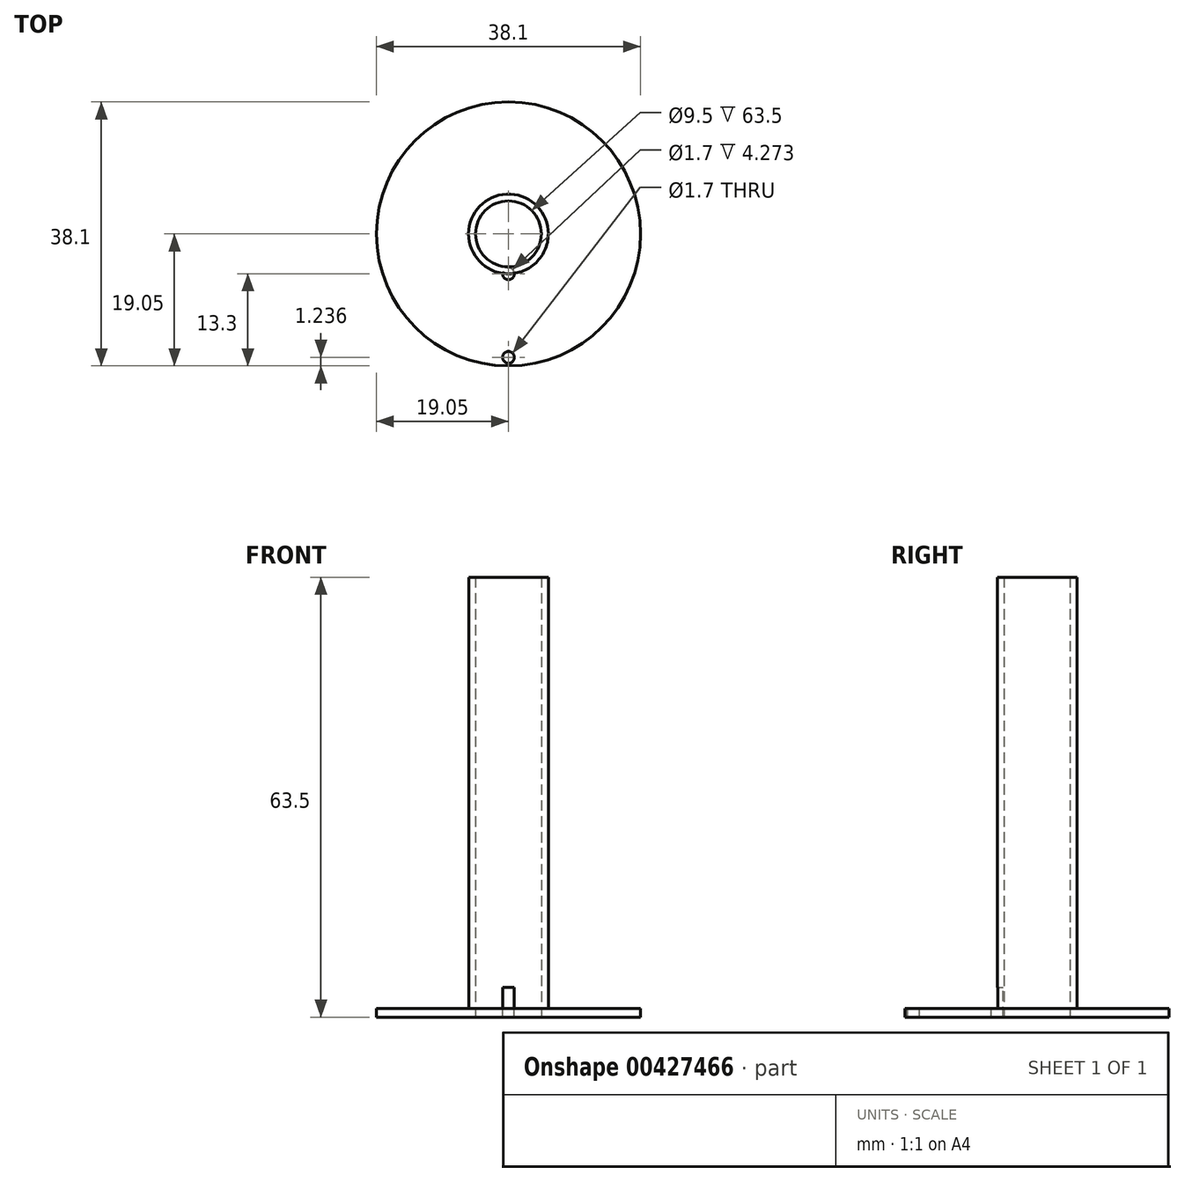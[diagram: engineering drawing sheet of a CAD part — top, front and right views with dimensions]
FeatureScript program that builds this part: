
annotation { "Feature Type Name" : "Feature", "Feature Type Description" : "" }
export const myFeature = defineFeature(function(context is Context, id is Id, definition is map)
    precondition{}
    {
        {
            var Q0;
            Q0=qCreatedBy(makeId("Top.planeOp"),FACE);
            var sketch = newSketch(context, id + "F0", { "sketchPlane" : qUnion([Q0])});
            skCircle(sketch, "E0", {"center": v(0, 0) * mm, "radius": 19.05 * mm});
            skCircle(sketch, "E1", {"center": v(0, 0) * mm, "radius": 4.75 * mm});
            skCircle(sketch, "E2", {"center": v(0, 0) * mm, "radius": 5.75 * mm});
            skSolve(sketch);
        }
        {
            var Q0;
            Q0 = qSketchRegion(id + "F0", true);
            var Q1;
            Q1=makeQuery(id+"F0.imprint","IMPRINT",FACE,{"disambiguationData":[TD([[makeQuery(id+"F0.imprint","IMPRINT",EDGE,{"derivedFrom":sQuery(id+"F0.wireOp",EDGE,"E1")}),-1.0]])]});
            extrude(context, id + "F1", {"entities" : qUnion([Q0, Q1]), "depth" : 1.25 * mm});
        }
        {
            var Q0;
            Q0=makeQuery(id+"F0.imprint","IMPRINT",FACE,{"disambiguationData":[TD([[makeQuery(id+"F0.imprint","IMPRINT",EDGE,{"derivedFrom":sQuery(id+"F0.wireOp",EDGE,"E1")}),-1.0]])]});
            extrude(context, id + "F2", {"entities" : qUnion([Q0]), "operationType" : NewBodyOperationType.ADD, "depth" : 63.5 * mm});
        }
        {
            var Q0;
            Q0=makeQuery(id+"F1.opExtrude","CAP_FACE",FACE,{"disambiguationData":[OSD([sQuery(id+"F0.wireOp",EDGE,"E0"),sQuery(id+"F0.wireOp",EDGE,"E1")])],"isStart":false});
            var sketch = newSketch(context, id + "F3", { "sketchPlane" : qUnion([Q0])});
            skCircle(sketch, "E3", {"center": v(0, -5.75) * mm, "radius": 0.85 * mm});
            skCircle(sketch, "E4", {"center": v(0, -17.81) * mm, "radius": 0.85 * mm});
            skSolve(sketch);
        }
        {
            var Q0;
            Q0 = qSketchRegion(id + "F3", true);
            extrude(context, id + "F4", {"entities" : qUnion([Q0]), "operationType" : NewBodyOperationType.REMOVE, "oppositeDirection" : true, "depth" : 25.4 * mm, "hasSecondDirection" : true, "secondDirectionOppositeDirection" : false, "secondDirectionDepth" : 3.02 * mm});
        }
    });
